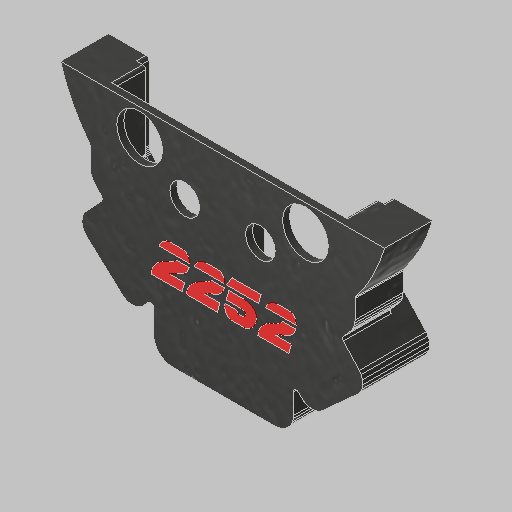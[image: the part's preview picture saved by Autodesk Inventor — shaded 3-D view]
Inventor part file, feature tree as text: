
AUTODESK INVENTOR PART (.ipt)
format: ipt  version: 2023.5 (Build 275446000, 446)  size: 3,544,064 bytes
history: native  units: in
note: dims shown in document units (in); Inventor stores cm internally (conversion verified against a paired STEP export)
features: other x10, extrude x9, projected_geometry x7, fillet x2, sketch x2, plane x1, reference x1
ambient origin geometry x8: Origin, YZ Plane, XZ Plane, XY Plane, X Axis, Y Axis, Z Axis, Center Point
bodies: Solid1 (feature_tree), Solid2 (feature_tree), Solid3 (feature_tree), Solid4 (feature_tree), Solid5 (feature_tree), Solid6 (feature_tree), Solid7 (feature_tree), Solid8 (feature_tree), Solid9 (feature_tree)
feature tree (32):
  other  "kraken-power-adapter.iam"
  other  "92916A325_Brass Washer.iam:1::SOLID.ipt:1"
  other  "93465A147_Brass Socket Head Screw.iam:1::SOLID_1.ipt:1"
  other  "92916A325_Brass Washer.iam:2::SOLID.ipt:1"
  other  "93465A147_Brass Socket Head Screw.iam:2::SOLID_1.ipt:1"
  other  "1335G1 IN HSG.iam:1::SOLID_2.ipt:1"
  other  "1335G1 IN HSG.iam:2::SOLID_2.ipt:1"
  other  "kraken-power-adapter PCB.ipt:1"
  plane  "Work Plane1"
  extrude  "Extrusion1"  [1 undecoded]
  extrude  "Extrusion3"  Depth=0.0787in
  extrude  "Extrusion4"  Depth=0.0787in
  extrude  "Extrusion5"  Depth=0.1181in
  extrude  "Extrusion6"  Depth=0.1181in
  fillet  "Fillet3"  Radius=0.1181in
  extrude  "Extrusion7"  Depth=0.0472in TaperAngle=0.0deg
  extrude  "Extrusion8"  Depth=1.0in TaperAngle=0.0deg
  fillet  "Fillet4"  Radius=1.0in
  extrude  "Extrusion9"  Depth=0.0472in
  extrude  "Extrusion10"  Depth=1.0in TaperAngle=0.0deg
  projected_geometry  "Projected Loop1"
  sketch  "Sketch5"  dims[d0=0.3937in d2=-0.3248in]
  projected_geometry  "Projected Loop4"
  projected_geometry  "Projected Loop5"
  reference  "Reference1"
  projected_geometry  "Projected Loop6"
  projected_geometry  "Projected Loop7"
  projected_geometry  "Projected Loop8"
  sketch  "Sketch9"  dims[d4=0.0787in d5=0.0787in d6=0.0787in d7=0.1181in d8=0.1181in d9=0.1181in d10=0.0472in d11=0.0in d15=1.0in d16=0.0in d18=1.0in d19=0.0472in d20=1.0in d21=0.0in d23=0.0197in d24=0.0039in d25=1.0in d26=0.0in d27=0.0197in d28=0.3189in d29=2.2835in d30=1.0in d31=0.0in d32=0.0787in d33=0.0079in d34=0.4528in d35=0.0in d36=0.4528in d37=0.0in d38=0.0197in d39=0.0079in d40=0.0in d41=0.0079in d42=0.0in d12=0.5in d13=0.0344in d14=0.5in]
  projected_geometry  "Projected Loop9"
  other  "Assembly1"
  other  "kraken-can-adapter:1"
note: 1 required parameter value undecoded (feature->parameter linkage not recoverable at this tier; creation-order binding heuristic only, values carry confidence <= 0.55)
